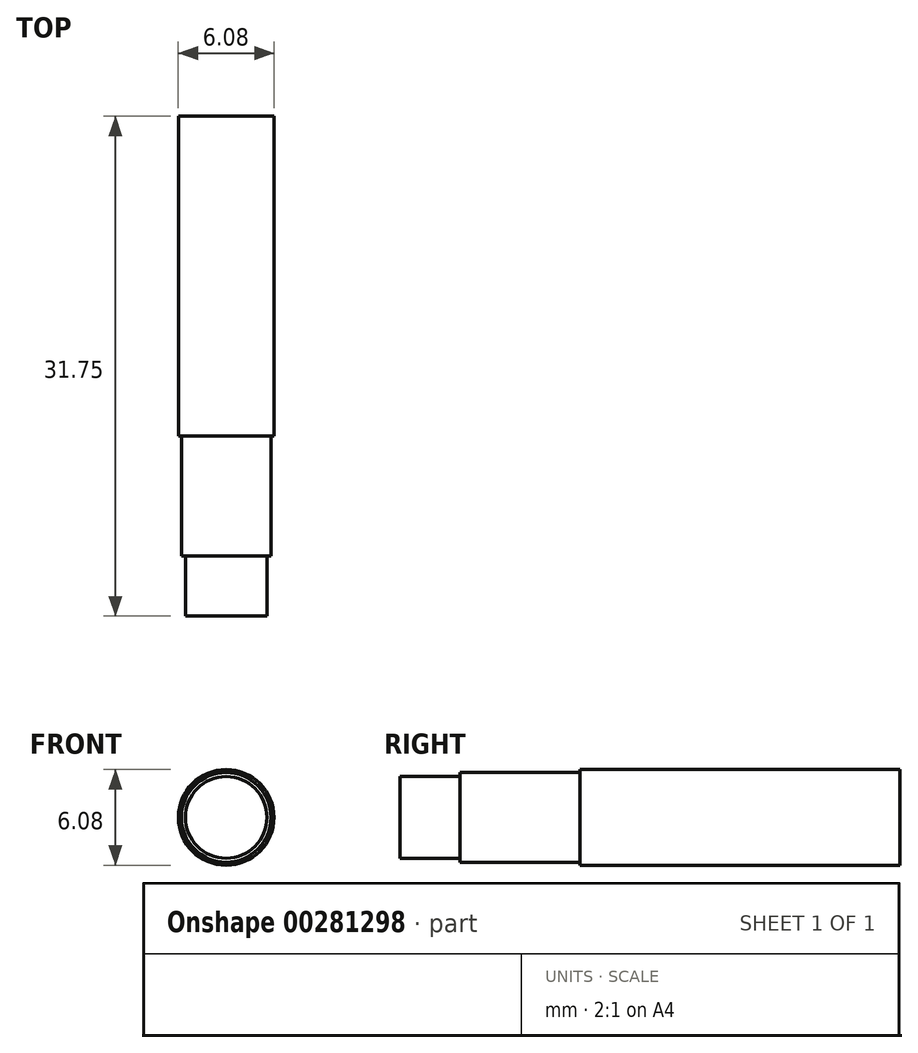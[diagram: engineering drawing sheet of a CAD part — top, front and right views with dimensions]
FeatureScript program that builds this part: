
annotation { "Feature Type Name" : "Feature", "Feature Type Description" : "" }
export const myFeature = defineFeature(function(context is Context, id is Id, definition is map)
    precondition{}
    {
        {
            var Q0;
            Q0=qCreatedBy(makeId("Front.planeOp"),FACE);
            var sketch = newSketch(context, id + "F0", { "sketchPlane" : qUnion([Q0])});
            skCircle(sketch, "E0", {"center": v(0, 0) * mm, "radius": 2.6 * mm});
            skSolve(sketch);
        }
        {
            var Q0;
            Q0=qCreatedBy(makeId("Front.planeOp"),FACE);
            var sketch = newSketch(context, id + "F1", { "sketchPlane" : qUnion([Q0])});
            skCircle(sketch, "E1", {"center": v(0, 0) * mm, "radius": 2.84 * mm});
            skSolve(sketch);
        }
        {
            var Q0;
            Q0=qCreatedBy(makeId("Front.planeOp"),FACE);
            var sketch = newSketch(context, id + "F2", { "sketchPlane" : qUnion([Q0])});
            skCircle(sketch, "E2", {"center": v(0, 0) * mm, "radius": 3.04 * mm});
            skSolve(sketch);
        }
        {
            var Q0;
            Q0 = qSketchRegion(id + "F0", true);
            extrude(context, id + "F3", {"entities" : qUnion([Q0]), "depth" : 31.75 * mm});
        }
        {
            var Q0;
            Q0 = qSketchRegion(id + "F1", true);
            extrude(context, id + "F4", {"entities" : qUnion([Q0]), "operationType" : NewBodyOperationType.ADD, "depth" : 27.94 * mm});
        }
        {
            var Q0;
            Q0 = qSketchRegion(id + "F2", true);
            extrude(context, id + "F5", {"entities" : qUnion([Q0]), "operationType" : NewBodyOperationType.ADD, "depth" : 20.32 * mm});
        }
    });
